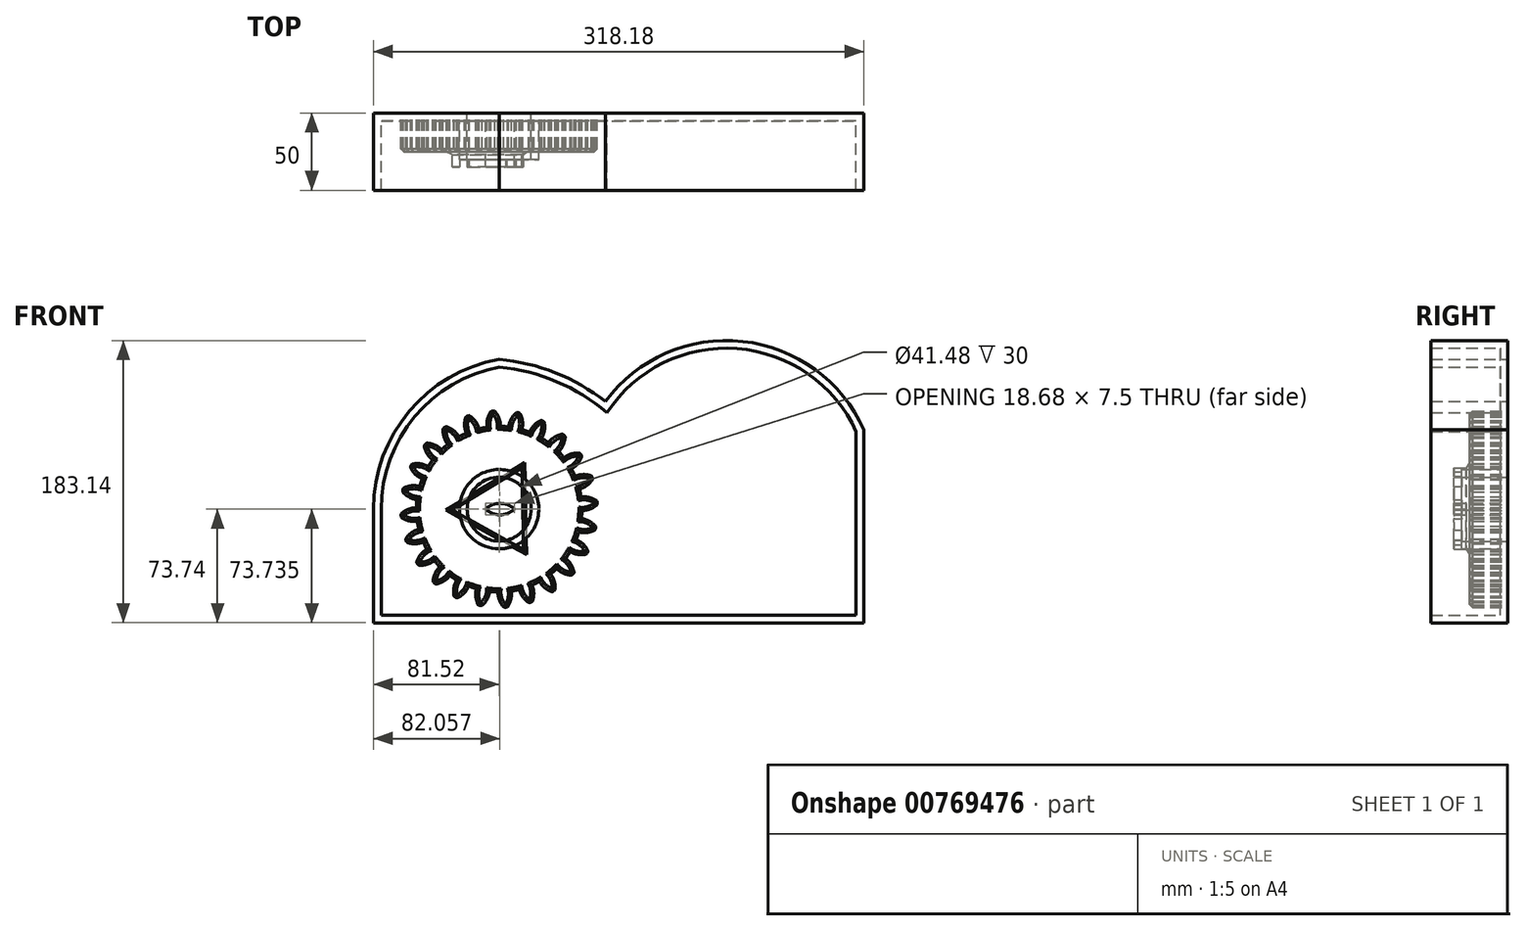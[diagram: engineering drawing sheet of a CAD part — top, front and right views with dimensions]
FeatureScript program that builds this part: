
annotation { "Feature Type Name" : "Feature", "Feature Type Description" : "" }
export const myFeature = defineFeature(function(context is Context, id is Id, definition is map)
    precondition{}
    {
        {
            var Q0;
            Q0=qCreatedBy(makeId("Front.planeOp"),FACE);
            var sketch = newSketch(context, id + "F0", { "sketchPlane" : qUnion([Q0])});
            skCircle(sketch, "E0", {"center": v(0, 0) * mm, "radius": 63.5 * mm, "construction": true});
            skCircle(sketch, "E1", {"center": v(0, 0) * mm, "radius": 58.67 * mm, "construction": true});
            skCircle(sketch, "E2", {"center": v(0, 0) * mm, "radius": 53.72 * mm});
            skLineSegment(sketch, "E3", {"start": v(0, 0) * mm, "end": v(0, 75.37) * mm, "construction": true});
            skLineSegment(sketch, "E4", {"start": v(0, 0) * mm, "end": v(-4.94, 75.37) * mm, "construction": true});
            skLineSegment(sketch, "E5", {"start": v(0, 58.67) * mm, "end": v(-55.05, 58.67) * mm, "construction": true});
            skLineSegment(sketch, "E6", {"start": v(0, 58.67) * mm, "end": v(-49.24, 40.75) * mm, "construction": true});
            skCircle(sketch, "E7", {"center": v(0, 0) * mm, "radius": 55.14 * mm, "construction": true});
            skCircle(sketch, "E8", {"center": v(0, 58.67) * mm, "radius": 14.6 * mm, "construction": true});
            skCircle(sketch, "E9", {"center": v(-13.72, 53.68) * mm, "radius": 14.6 * mm, "construction": true});
            skArc(sketch, "E10", {"start": v(0, 58.67) * mm, "mid": v(-1.2, 61.2) * mm, "end": v(-2.86, 63.44) * mm});
            skArc(sketch, "E11", {"start": v(0.88, 53.71) * mm, "mid": v(0.67, 56.23) * mm, "end": v(0, 58.67) * mm});
            skArc(sketch, "E12.MirrorCS", {"start": v(-7.66, 58.17) * mm, "mid": v(-6.8, 60.82) * mm, "end": v(-5.45, 63.27) * mm});
            skArc(sketch, "E13.MirrorCS", {"start": v(-7.88, 53.14) * mm, "mid": v(-8, 55.67) * mm, "end": v(-7.66, 58.17) * mm});
            skArc(sketch, "E14", {"start": v(-2.86, 63.44) * mm, "mid": v(-4.17, 63.66) * mm, "end": v(-5.45, 63.27) * mm});
            skCircle(sketch, "E15.cCircle", {"center": v(0, 0) * mm, "radius": 30.5 * mm, "construction": true});
            skLineSegment(sketch, "E15.0", {"start": v(15.78, -26.11) * mm, "end": v(-30.5, -0.61) * mm});
            skLineSegment(sketch, "E15.1", {"start": v(-30.5, -0.61) * mm, "end": v(14.72, 26.72) * mm});
            skLineSegment(sketch, "E15.2", {"start": v(14.72, 26.72) * mm, "end": v(15.78, -26.11) * mm});
            skArc(sketch, "E16", {"start": v(9.88, 0) * mm, "mid": v(0.54, 3.74) * mm, "end": v(-8.8, 0) * mm});
            skArc(sketch, "E17", {"start": v(-8.8, 0) * mm, "mid": v(0.54, -3.75) * mm, "end": v(9.88, 0) * mm});
            skSolve(sketch);
        }
        {
            var Q0;
            {var subQ0=sQuery(id+"F0.wireOp",EDGE,"E2");var subQ1=makeQuery(id+"F0.imprint","INTERSECT",VERTEX,{"derivedFrom":[subQ0,sQuery(id+"F0.wireOp",EDGE,"E11")]});Q0=makeQuery(id+"F0.imprint","IMPRINT",FACE,{"disambiguationData":[TD([[makeQuery(id+"F0.imprint","IMPRINT",EDGE,{"disambiguationData":[TD([[subQ1,-1.0]])],"derivedFrom":subQ0}),1.0]])]});}
            var Q1;
            Q1=makeQuery(id+"F0.imprint","IMPRINT",FACE,{"disambiguationData":[TD([[makeQuery(id+"F0.imprint","IMPRINT",EDGE,{"derivedFrom":sQuery(id+"F0.wireOp",EDGE,"E10")}),1.0]])]});
            extrude(context, id + "F1", {"entities" : qUnion([Q0, Q1]), "depth" : 25 * mm, "offsetDistance" : 25 * mm});
        }
        {
            var Q0;
            Q0=makeQuery(id+"F1.opExtrude","SWEPT_BODY",BODY,{"disambiguationData":[OSD([sQuery(id+"F0.wireOp",EDGE,"E2"),sQuery(id+"F0.wireOp",EDGE,"E10"),sQuery(id+"F0.wireOp",EDGE,"E11"),sQuery(id+"F0.wireOp",EDGE,"E12.MirrorCS"),sQuery(id+"F0.wireOp",EDGE,"E13.MirrorCS"),sQuery(id+"F0.wireOp",EDGE,"E14")])]});
            var Q1;
            Q1=makeQuery(id+"F1.opExtrude","SWEPT_FACE",FACE,{"disambiguationData":[OSD([sQuery(id+"F0.wireOp",EDGE,"E2")])]});
            circularPattern(context, id + "F2", {"entities" : qUnion([Q0]), "axis" : qUnion([Q1]), "angle" : 360 * degree, "instanceCount" : 24, "equalSpace" : true});
        }
        {
            var Q0;
            Q0=makeQuery(id+"F0.imprint","IMPRINT",FACE,{"disambiguationData":[TD([[makeQuery(id+"F0.imprint","IMPRINT",EDGE,{"derivedFrom":sQuery(id+"F0.wireOp",EDGE,"E15.0")}),-1.0]])]});
            extrude(context, id + "F3", {"entities" : qUnion([Q0]), "operationType" : NewBodyOperationType.ADD, "depth" : 35 * mm, "offsetDistance" : 25 * mm});
        }
        {
            var Q0;
            {var subQ0=makeQuery(id+"F1.opExtrude","CAP_FACE",FACE,{"disambiguationData":[OSD([sQuery(id+"F0.wireOp",EDGE,"E2"),sQuery(id+"F0.wireOp",EDGE,"E10"),sQuery(id+"F0.wireOp",EDGE,"E11"),sQuery(id+"F0.wireOp",EDGE,"E12.MirrorCS"),sQuery(id+"F0.wireOp",EDGE,"E13.MirrorCS"),sQuery(id+"F0.wireOp",EDGE,"E14"),sQuery(id+"F0.wireOp",EDGE,"E15.0"),sQuery(id+"F0.wireOp",EDGE,"E15.1"),sQuery(id+"F0.wireOp",EDGE,"E15.2")])],"isStart":false});Q0=makeQuery(id+"F3.boolean.opBoolean","MERGE",FACE,{"derivedFrom":[subQ0,makeQuery(id+"F2.opPattern","COPY",FACE,{"derivedFrom":subQ0,"instanceName":"1"}),makeQuery(id+"F2.opPattern","COPY",FACE,{"derivedFrom":subQ0,"instanceName":"2"}),makeQuery(id+"F2.opPattern","COPY",FACE,{"derivedFrom":subQ0,"instanceName":"3"}),makeQuery(id+"F2.opPattern","COPY",FACE,{"derivedFrom":subQ0,"instanceName":"4"}),makeQuery(id+"F2.opPattern","COPY",FACE,{"derivedFrom":subQ0,"instanceName":"5"}),makeQuery(id+"F2.opPattern","COPY",FACE,{"derivedFrom":subQ0,"instanceName":"6"}),makeQuery(id+"F2.opPattern","COPY",FACE,{"derivedFrom":subQ0,"instanceName":"7"}),makeQuery(id+"F2.opPattern","COPY",FACE,{"derivedFrom":subQ0,"instanceName":"8"}),makeQuery(id+"F2.opPattern","COPY",FACE,{"derivedFrom":subQ0,"instanceName":"9"}),makeQuery(id+"F2.opPattern","COPY",FACE,{"derivedFrom":subQ0,"instanceName":"10"}),makeQuery(id+"F2.opPattern","COPY",FACE,{"derivedFrom":subQ0,"instanceName":"11"}),makeQuery(id+"F2.opPattern","COPY",FACE,{"derivedFrom":subQ0,"instanceName":"12"}),makeQuery(id+"F2.opPattern","COPY",FACE,{"derivedFrom":subQ0,"instanceName":"13"}),makeQuery(id+"F2.opPattern","COPY",FACE,{"derivedFrom":subQ0,"instanceName":"14"}),makeQuery(id+"F2.opPattern","COPY",FACE,{"derivedFrom":subQ0,"instanceName":"15"}),makeQuery(id+"F2.opPattern","COPY",FACE,{"derivedFrom":subQ0,"instanceName":"16"}),makeQuery(id+"F2.opPattern","COPY",FACE,{"derivedFrom":subQ0,"instanceName":"17"}),makeQuery(id+"F2.opPattern","COPY",FACE,{"derivedFrom":subQ0,"instanceName":"18"}),makeQuery(id+"F2.opPattern","COPY",FACE,{"derivedFrom":subQ0,"instanceName":"19"}),makeQuery(id+"F2.opPattern","COPY",FACE,{"derivedFrom":subQ0,"instanceName":"20"}),makeQuery(id+"F2.opPattern","COPY",FACE,{"derivedFrom":subQ0,"instanceName":"21"}),makeQuery(id+"F2.opPattern","COPY",FACE,{"derivedFrom":subQ0,"instanceName":"22"}),makeQuery(id+"F2.opPattern","COPY",FACE,{"derivedFrom":subQ0,"instanceName":"23"})]});}
            chamfer(context, id + "F4", {"entities" : qUnion([Q0]), "width" : 2 * mm, "tangentPropagation" : true});
        }
        {
            var Q0;
            Q0=qCreatedBy(makeId("Front.planeOp"),FACE);
            var sketch = newSketch(context, id + "F5", { "sketchPlane" : qUnion([Q0])});
            skLineSegment(sketch, "E18", {"start": v(-81.52, -73.74) * mm, "end": v(236.66, -73.74) * mm});
            skLineSegment(sketch, "E19", {"start": v(236.66, -73.74) * mm, "end": v(236.66, 51.44) * mm});
            skLineSegment(sketch, "E20", {"start": v(-81.52, -73.74) * mm, "end": v(-81.52, 0) * mm});
            skArc(sketch, "E21", {"start": v(0, 97.18) * mm, "mid": v(-58.44, 63.42) * mm, "end": v(-81.52, 0) * mm});
            skArc(sketch, "E22", {"start": v(68.94, 69.9) * mm, "mid": v(36.43, 88.49) * mm, "end": v(0, 97.18) * mm});
            skArc(sketch, "E23", {"start": v(236.66, 51.44) * mm, "mid": v(158.1, 108.8) * mm, "end": v(68.94, 69.9) * mm});
            skCircle(sketch, "E24", {"center": v(0, 0) * mm, "radius": 20.74 * mm});
            skSolve(sketch);
        }
        {
            var Q0;
            Q0=makeQuery(id+"F5.imprint","IMPRINT",FACE,{"disambiguationData":[TD([[makeQuery(id+"F5.imprint","IMPRINT",EDGE,{"derivedFrom":sQuery(id+"F5.wireOp",EDGE,"E18")}),1.0]])]});
            extrude(context, id + "F6", {"entities" : qUnion([Q0]), "depth" : 50 * mm, "offsetDistance" : 25 * mm});
        }
        {
            var Q0;
            Q0=makeQuery(id+"F6.opExtrude","CAP_FACE",FACE,{"disambiguationData":[OSD([sQuery(id+"F5.wireOp",EDGE,"E18"),sQuery(id+"F5.wireOp",EDGE,"E19"),sQuery(id+"F5.wireOp",EDGE,"E20"),sQuery(id+"F5.wireOp",EDGE,"E21"),sQuery(id+"F5.wireOp",EDGE,"E22"),sQuery(id+"F5.wireOp",EDGE,"E23")])],"isStart":false});
            shell(context, id + "F7", {"entities" : qUnion([Q0]), "thickness" : 5 * mm});
        }
        {
            var Q0;
            {var subQ0=sQuery(id+"F5.wireOp",EDGE,"E24");var subQ1=sQuery(id+"F5.wireOp",EDGE,"E23");var subQ2=sQuery(id+"F5.wireOp",EDGE,"E22");var subQ3=sQuery(id+"F5.wireOp",EDGE,"E21");var subQ4=sQuery(id+"F5.wireOp",EDGE,"E20");var subQ5=sQuery(id+"F5.wireOp",EDGE,"E19");var subQ6=sQuery(id+"F5.wireOp",EDGE,"E18");Q0=makeQuery(id+"F7.opShell","OFFSET_FACE",FACE,{"disambiguationData":[OSD([subQ6,subQ5,subQ4,subQ3,subQ2,subQ1,subQ0]),TDD([makeQuery(id+"F6.opExtrude","CAP_FACE",FACE,{"disambiguationData":[OSD([subQ6,subQ5,subQ4,subQ3,subQ2,subQ1,subQ0])],"isStart":false})])]});}
            extrude(context, id + "F8", {"entities" : qUnion([Q0]), "operationType" : NewBodyOperationType.REMOVE, "oppositeDirection" : true, "depth" : 20 * mm, "offsetDistance" : 25 * mm});
        }
    });
